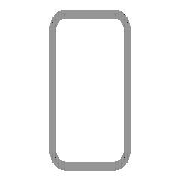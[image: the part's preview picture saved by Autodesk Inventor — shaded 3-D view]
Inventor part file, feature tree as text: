
AUTODESK INVENTOR PART (.ipt)
format: ipt  version: 2025 (Build 290162010, 162A)  size: 134,656 bytes
history: native  units: mm (DEFAULTED — no unit token found)
features: other x4, sketch x1, plane x1
ambient origin geometry x8: Origin, YZ Plane, XZ Plane, XY Plane, X Axis, Y Axis, Z Axis, Center Point
bodies: Solid1 (feature_tree), Body (feature_tree)
feature tree (6):
  parser-record x1  (decoder bookkeeping rows leaked as tree rows — omitted from the tree; the rows remain in map.json)
  other  "Driven Length"
  other  "Start Plane"
  other  "End Plane"
  sketch  "Sketch3"  dims[d3=3111.269837mm d4=0.0mm d7=4.0mm d9=20.0mm d11=40.0mm d12=2.0mm d13=-0.0mm d14=3111.269837mm d15=10.0mm d16=20.0mm d17=90.0deg d18=3111.269837mm]
  plane  "Work Plane3"
